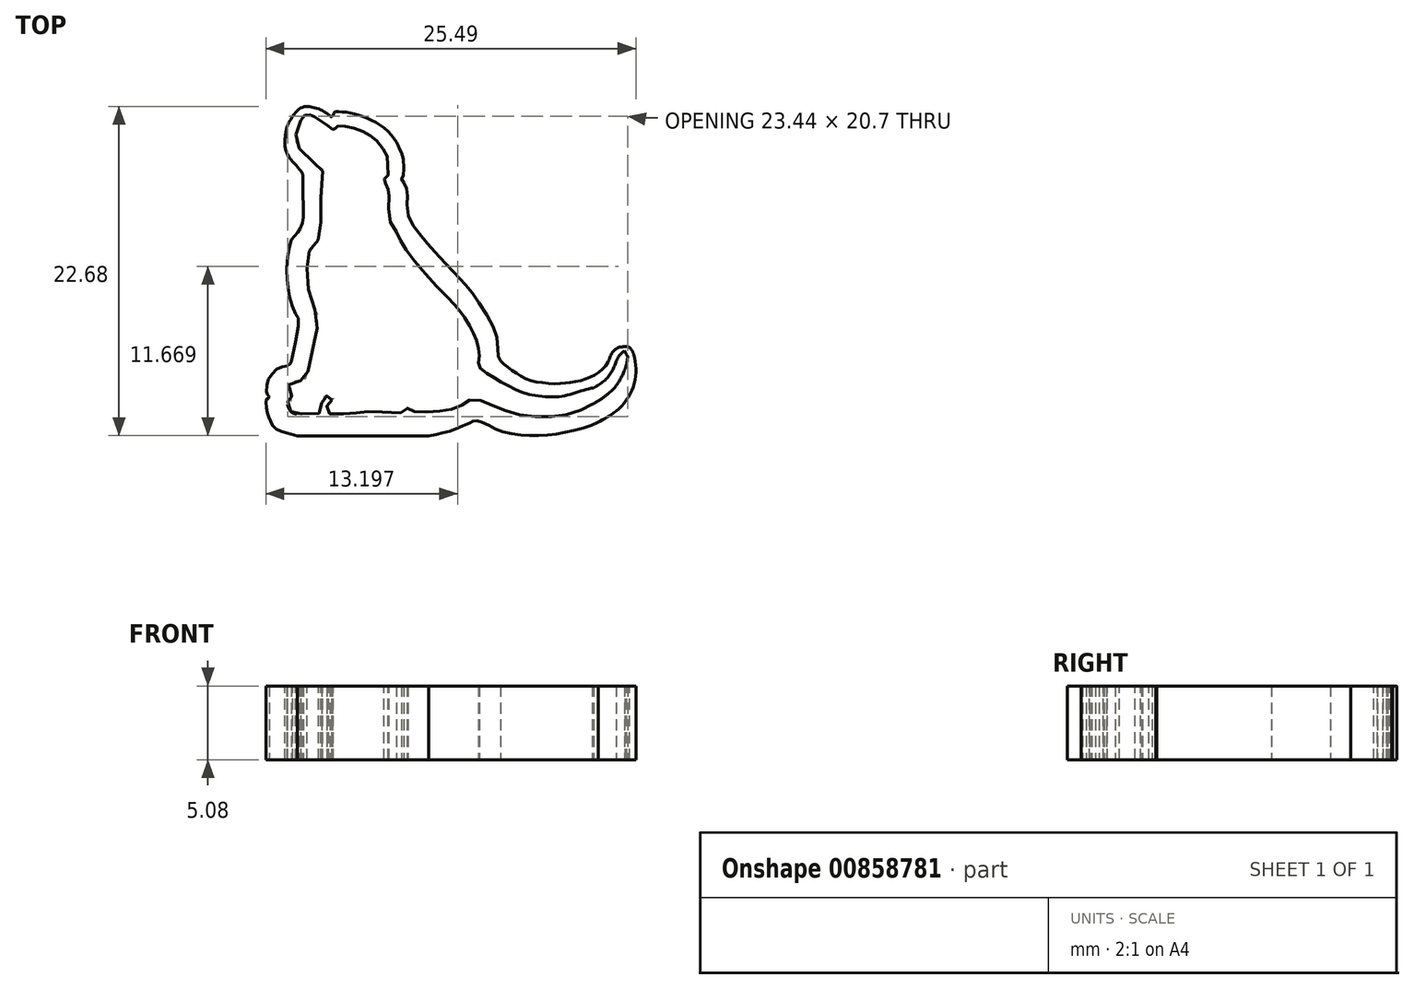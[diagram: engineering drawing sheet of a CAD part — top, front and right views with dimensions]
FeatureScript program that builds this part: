
annotation { "Feature Type Name" : "Feature", "Feature Type Description" : "" }
export const myFeature = defineFeature(function(context is Context, id is Id, definition is map)
    precondition{}
    {
        {
            var Q0;
            Q0=qCreatedBy(makeId("Top.planeOp"),FACE);
            var sketch = newSketch(context, id + "F0", { "sketchPlane" : qUnion([Q0])});
            skFitSpline(sketch, "E0", {"points": [v(-18.64, 26.8) * mm, v(-17.67, 25.17) * mm, v(-15, 22.17) * mm, v(-14.18, 21.25) * mm, v(-13.45, 20.1) * mm, v(-13.07, 19.16) * mm, v(-12.93, 18.19) * mm, v(-12.96, 17.55) * mm, v(-12.13, 16.92) * mm, v(-11.21, 16.35) * mm, v(-10.31, 15.9) * mm, v(-9.5, 15.6) * mm, v(-8.22, 15.45) * mm, v(-7.3, 15.48) * mm, v(-6.28, 15.74) * mm, v(-5.41, 16) * mm, v(-4.68, 16.04) * mm, v(-4.2, 15.74) * mm, v(-4.11, 15.31) * mm, v(-4.47, 14.84) * mm], "startDerivative": vector(10.05, -20.8) * mm, "endDerivative": vector(-11.78, -11.66) * mm});
            skFitSpline(sketch, "E1", {"points": [v(-9.5, 15.6) * mm, v(-8.72, 15.47) * mm, v(-7.72, 15.38) * mm, v(-6.88, 15.45) * mm, v(-6.21, 15.6) * mm, v(-5.62, 15.8) * mm, v(-5.06, 15.91) * mm, v(-4.74, 15.84) * mm, v(-4.58, 15.6) * mm, v(-4.64, 15.45) * mm, v(-4.81, 15.22) * mm, v(-5.13, 14.94) * mm, v(-5.65, 14.65) * mm, v(-6.3, 14.4) * mm, v(-7.1, 14.19) * mm, v(-7.82, 14.1) * mm, v(-8.74, 14.07) * mm, v(-9.5, 14.11) * mm, v(-10.51, 14.3) * mm, v(-11.1, 14.5) * mm, v(-11.64, 14.71) * mm, v(-12.33, 15) * mm, v(-12.8, 15.2) * mm, v(-13.18, 15.28) * mm, v(-13.65, 15.21) * mm, v(-13.89, 15.06) * mm, v(-14.13, 14.88) * mm, v(-14.44, 14.71) * mm, v(-14.94, 14.56) * mm, v(-15.47, 14.48) * mm, v(-16.02, 14.43) * mm, v(-16.6, 14.4) * mm, v(-17.18, 14.43) * mm, v(-17.55, 14.5) * mm, v(-17.68, 14.65) * mm, v(-17.88, 14.66) * mm, v(-17.96, 14.47) * mm, v(-18.17, 14.36) * mm, v(-19.22, 14.37) * mm, v(-20.18, 14.41) * mm, v(-20.7, 14.43) * mm, v(-21.2, 14.36) * mm, v(-21.69, 14.3) * mm, v(-22.28, 14.26) * mm, v(-23, 14.28) * mm, v(-23.35, 14.32) * mm, v(-23.43, 14.63) * mm, v(-23.4, 14.91) * mm, v(-23.24, 15.12) * mm, v(-23.07, 15.23) * mm], "startDerivative": vector(23.7, -7.27) * mm, "endDerivative": vector(13.55, 6.78) * mm});
            skFitSpline(sketch, "E2", {"points": [v(-18.64, 26.8) * mm, v(-19.13, 27.71) * mm, v(-19.15, 29.17) * mm, v(-19.16, 29.6) * mm, v(-19.26, 29.95) * mm, v(-19.43, 30.25) * mm, v(-19.49, 30.38) * mm, v(-19.43, 30.5) * mm, v(-19.26, 30.6) * mm, v(-19.2, 31.05) * mm, v(-19.26, 31.93) * mm, v(-19.33, 32.16) * mm, v(-19.82, 32.9) * mm, v(-20.2, 33.28) * mm, v(-20.67, 33.61) * mm, v(-21.2, 33.84) * mm, v(-21.83, 34.02) * mm, v(-22.38, 34.1) * mm, v(-22.69, 34.1) * mm, v(-22.78, 34.08) * mm, v(-22.83, 34) * mm, v(-22.85, 33.9) * mm, v(-22.92, 33.87) * mm, v(-23.02, 33.88) * mm, v(-23.16, 33.98) * mm, v(-24.31, 34.78) * mm, v(-24.49, 34.85) * mm, v(-24.67, 34.9) * mm, v(-24.86, 34.88) * mm, v(-25.01, 34.78) * mm, v(-25.2, 34.53) * mm, v(-25.25, 34.43) * mm, v(-25.24, 34.3) * mm, v(-25.23, 34.18) * mm], "startDerivative": vector(-11.38, 14.65) * mm, "endDerivative": vector(0.42, -6.75) * mm});
            skFitSpline(sketch, "E3", {"points": [v(-25.2, 34.53) * mm, v(-25.43, 34.12) * mm, v(-25.55, 33.7) * mm, v(-25.57, 33.14) * mm, v(-25.47, 32.8) * mm, v(-25.05, 32.28) * mm, v(-24.37, 31.64) * mm, v(-23.88, 31.24) * mm, v(-23.75, 31.13) * mm, v(-23.71, 30.96) * mm, v(-23.81, 29.43) * mm, v(-23.83, 27.82) * mm, v(-23.86, 27.12) * mm, v(-23.99, 26.36) * mm, v(-24.2, 26) * mm, v(-24.5, 25.67) * mm, v(-24.72, 25.34) * mm, v(-24.79, 24.67) * mm, v(-24.75, 23.66) * mm, v(-24.68, 22.74) * mm, v(-24.45, 21.84) * mm, v(-24.06, 21.1) * mm, v(-24.02, 20.72) * mm, v(-24.75, 17.1) * mm, v(-24.88, 16.75) * mm, v(-25.02, 16.6) * mm, v(-25.46, 16.55) * mm, v(-25.84, 16.43) * mm, v(-26.05, 16.28) * mm, v(-26.1, 15.69) * mm, v(-25.95, 15.55) * mm, v(-25.8, 15.44) * mm, v(-25.8, 15.29) * mm, v(-25.91, 15.22) * mm, v(-26.08, 15.2) * mm, v(-26.14, 14.98) * mm, v(-26.1, 14.74) * mm, v(-25.97, 14.52) * mm, v(-25.8, 14.35) * mm, v(-25.63, 14.29) * mm, v(-25.36, 14.27) * mm, v(-24.45, 14.27) * mm, v(-24.02, 14.29) * mm, v(-23.87, 14.38) * mm, v(-23.84, 14.72) * mm, v(-23.78, 15.01) * mm, v(-23.63, 15.25) * mm, v(-23.6, 15.46) * mm, v(-23.52, 15.52) * mm, v(-23.34, 15.52) * mm, v(-23.16, 15.45) * mm, v(-22.98, 15.35) * mm, v(-23.07, 15.23) * mm], "startDerivative": vector(-12.69, -20.47) * mm, "endDerivative": vector(-12.96, -11.1) * mm});
            skFitSpline(sketch, "E4", {"points": [v(-23.08, 16.7) * mm, v(-21.94, 19.17) * mm, v(-21.85, 19.47) * mm, v(-21.79, 19.58) * mm, v(-21.64, 19.6) * mm, v(-21.56, 19.53) * mm, v(-21.54, 19.42) * mm, v(-21.46, 19.35) * mm, v(-21.26, 19.2) * mm, v(-21.06, 19.1) * mm, v(-20.96, 19.02) * mm, v(-20.97, 18.84) * mm, v(-21.11, 18.68) * mm, v(-21.16, 18.5) * mm, v(-21.17, 18.18) * mm, v(-21.1, 17.9) * mm, v(-20.94, 17.57) * mm, v(-20.66, 17.12) * mm, v(-20.63, 16.86) * mm, v(-20.8, 16.71) * mm, v(-21.1, 16.62) * mm, v(-21.6, 16.57) * mm, v(-22.32, 16.56) * mm, v(-22.93, 16.5) * mm, v(-23.08, 16.53) * mm, v(-23.13, 16.58) * mm, v(-23.08, 16.7) * mm]});
            skFitSpline(sketch, "E5", {"points": [v(-21.86, 15.57) * mm, v(-19.82, 15.8) * mm, v(-19.69, 15.8) * mm, v(-19.62, 15.6) * mm, v(-19.68, 15.5) * mm, v(-20.03, 15.34) * mm, v(-20.57, 15.23) * mm, v(-21.23, 15.2) * mm, v(-21.7, 15.28) * mm, v(-21.84, 15.34) * mm], "startDerivative": vector(10.76, 1.04) * mm, "endDerivative": vector(-1.73, 0.9) * mm});
            skFitSpline(sketch, "E6", {"points": [v(-21.84, 15.34) * mm, v(-21.88, 15.44) * mm, v(-21.86, 15.57) * mm], "startDerivative": vector(-0.1, 0.21) * mm, "endDerivative": vector(0.07, 0.25) * mm});
            skPoint(sketch, "E7.1.internal.orphan", {"position": v(-24.41, 31.05) * mm});
            skPoint(sketch, "E8.7.internal.snap0", {"position": v(-11.42, 13.4) * mm});
            skPoint(sketch, "E8.8.internal.snap0", {"position": v(-11.42, 13.45) * mm});
            skFitSpline(sketch, "E9.trimOffspring", {"points": [v(-11.33, 13.53) * mm, v(-12.83, 14.23) * mm, v(-13.03, 14.3) * mm, v(-13.4, 14.32) * mm, v(-13.63, 14.24) * mm, v(-14.53, 13.84) * mm, v(-15.5, 13.53) * mm, v(-18.01, 13.4) * mm, v(-24.51, 13.45) * mm, v(-26.14, 14.16) * mm], "startDerivative": vector(-14.88, 6.54) * mm, "endDerivative": vector(-9.16, 7.25) * mm});
            skFitSpline(sketch, "E10.trimOffspring", {"points": [v(-25.27, 17.31) * mm, v(-25.4, 17.12) * mm, v(-25.87, 17.05) * mm, v(-26.28, 16.9) * mm, v(-26.59, 16.65) * mm, v(-26.82, 16.2) * mm, v(-26.85, 15.72) * mm, v(-26.81, 15.56) * mm, v(-26.7, 15.48) * mm, v(-26.7, 15.43) * mm, v(-26.72, 15.35) * mm, v(-26.78, 15.29) * mm, v(-26.81, 15.27) * mm, v(-26.83, 15.23) * mm, v(-26.84, 15.17) * mm, v(-26.79, 14.82) * mm, v(-26.75, 14.37) * mm, v(-26.31, 13.9) * mm, v(-24.51, 13.45) * mm], "startDerivative": vector(-1.67, -4.49) * mm, "endDerivative": vector(14.6, -2.5) * mm});
            skFitSpline(sketch, "E11", {"points": [v(-6.48, 17.1) * mm, v(-7.36, 16.99) * mm, v(-8.18, 16.99) * mm, v(-9.04, 17.07) * mm, v(-9.92, 17.26) * mm, v(-10.74, 17.6) * mm, v(-11.45, 17.93) * mm, v(-11.59, 18.15) * mm, v(-11.63, 18.41) * mm, v(-11.7, 19.47) * mm, v(-12.19, 20.74) * mm, v(-13.2, 22.3) * mm, v(-13.91, 23.21) * mm, v(-16.3, 25.78) * mm, v(-17.26, 26.98) * mm, v(-17.78, 27.85) * mm, v(-17.88, 29.02) * mm, v(-17.86, 29.53) * mm, v(-18.02, 30.04) * mm, v(-18.2, 30.28) * mm, v(-18.27, 30.42) * mm, v(-18.25, 30.57) * mm, v(-18.17, 30.66) * mm, v(-18.13, 31.07) * mm, v(-18.18, 31.92) * mm, v(-18.28, 32.28) * mm, v(-18.85, 33.1) * mm, v(-19.38, 33.72) * mm, v(-20.14, 34.24) * mm, v(-20.86, 34.57) * mm, v(-21.64, 34.79) * mm, v(-22.34, 34.89) * mm, v(-22.74, 34.9) * mm, v(-22.87, 34.85) * mm, v(-22.9, 34.77) * mm, v(-22.92, 34.69) * mm, v(-22.94, 34.61) * mm, v(-23.03, 34.57) * mm, v(-23.1, 34.57) * mm, v(-23.2, 34.63) * mm, v(-23.38, 34.79) * mm], "startDerivative": vector(-28.78, -4.16) * mm, "endDerivative": vector(-12.37, 11.09) * mm});
            skFitSpline(sketch, "E12", {"points": [v(-18.28, 32.28) * mm, v(-18.57, 32.86) * mm, v(-19, 33.53) * mm, v(-19.88, 34.26) * mm, v(-20.7, 34.66) * mm, v(-21.58, 34.97) * mm, v(-22.33, 35.08) * mm, v(-22.76, 35.1) * mm, v(-22.88, 35.07) * mm, v(-22.95, 34.96) * mm, v(-23, 34.85) * mm, v(-23.04, 34.78) * mm, v(-23.12, 34.77) * mm, v(-23.16, 34.77) * mm, v(-23.22, 34.84) * mm, v(-23.3, 34.9) * mm, v(-23.53, 35.07) * mm], "startDerivative": vector(-3.23, 6.6) * mm, "endDerivative": vector(-4.35, 3.68) * mm});
            skFitSpline(sketch, "E13", {"points": [v(-23.04, 34.78) * mm, v(-23.06, 34.77) * mm, v(-23.1, 34.77) * mm, v(-23.14, 34.79) * mm, v(-23.4, 34.97) * mm, v(-23.76, 35.18) * mm, v(-24.11, 35.43) * mm, v(-24.54, 35.57) * mm, v(-24.95, 35.59) * mm, v(-25.4, 35.53) * mm, v(-25.8, 35.28) * mm, v(-26.19, 34.91) * mm, v(-26.45, 34.47) * mm, v(-26.72, 33.71) * mm, v(-26.75, 32.98) * mm, v(-26.57, 32.2) * mm, v(-26.07, 31.53) * mm, v(-25.4, 31) * mm, v(-25.12, 30.88) * mm, v(-25.08, 30.74) * mm, v(-25.07, 30.57) * mm, v(-25.07, 29.48) * mm, v(-25.05, 27.86) * mm, v(-25.12, 27.36) * mm, v(-25.28, 27.01) * mm, v(-25.4, 26.8) * mm, v(-25.6, 26.59) * mm, v(-25.8, 26.4) * mm, v(-25.95, 25.99) * mm, v(-26.1, 25.28) * mm, v(-26.17, 24.68) * mm, v(-26.15, 23.63) * mm, v(-26.07, 22.7) * mm, v(-25.8, 21.62) * mm, v(-25.47, 21.02) * mm, v(-25.37, 20.78) * mm, v(-25.88, 17.9) * mm], "startDerivative": vector(-3.52, -1.33) * mm, "endDerivative": vector(-12.4, -56.43) * mm});
            skFitSpline(sketch, "E14", {"points": [v(-25.88, 17.9) * mm, v(-25.93, 17.73) * mm, v(-26.03, 17.63) * mm, v(-26.34, 17.56) * mm, v(-26.8, 17.41) * mm, v(-27.3, 16.88) * mm, v(-27.55, 16.35) * mm, v(-27.58, 15.74) * mm, v(-27.54, 15.61) * mm, v(-27.45, 15.55) * mm, v(-27.42, 15.51) * mm, v(-27.42, 15.42) * mm, v(-27.48, 15.34) * mm, v(-27.53, 15.31) * mm, v(-27.6, 15.28) * mm, v(-27.62, 15.2) * mm, v(-27.6, 14.84) * mm, v(-27.54, 14.37) * mm, v(-27.46, 14.1) * mm, v(-27.33, 13.82) * mm, v(-27.18, 13.48) * mm, v(-26.9, 13.22) * mm, v(-26.42, 13.01) * mm, v(-26.1, 12.92) * mm, v(-25.44, 12.77) * mm], "startDerivative": vector(-1.3, -5.64) * mm, "endDerivative": vector(11.14, -2.6) * mm});
            skLineSegment(sketch, "E15", {"start": v(-25.44, 12.77) * mm, "end": v(-16.4, 12.77) * mm});
            skFitSpline(sketch, "E16", {"points": [v(-16.4, 12.77) * mm, v(-15.63, 12.92) * mm, v(-15, 13.08) * mm, v(-14.33, 13.31) * mm, v(-13.57, 13.67) * mm, v(-13.43, 13.74) * mm, v(-13.13, 13.8) * mm, v(-12.95, 13.77) * mm, v(-12.2, 13.45) * mm, v(-11.48, 13.1) * mm, v(-10.27, 12.85) * mm, v(-9.14, 12.77) * mm, v(-7.98, 12.84) * mm, v(-6.82, 13.04) * mm, v(-5.6, 13.35) * mm, v(-4.74, 13.7) * mm, v(-4.16, 13.95) * mm, v(-3.3, 14.47) * mm, v(-2.28, 15.31) * mm], "startDerivative": vector(14.64, 2.55) * mm, "endDerivative": vector(13.76, 11.69) * mm});
            skFitSpline(sketch, "E17.trimOffspring", {"points": [v(-23.04, 34.78) * mm, v(-23.06, 34.77) * mm, v(-23.1, 34.77) * mm, v(-23.14, 34.79) * mm, v(-23.4, 34.97) * mm, v(-23.76, 35.18) * mm, v(-24.11, 35.43) * mm, v(-24.54, 35.57) * mm, v(-24.95, 35.59) * mm, v(-25.4, 35.53) * mm, v(-25.8, 35.28) * mm, v(-26.19, 34.91) * mm, v(-26.45, 34.47) * mm, v(-26.72, 33.71) * mm, v(-26.75, 32.98) * mm, v(-26.57, 32.2) * mm, v(-26.07, 31.53) * mm, v(-25.4, 31) * mm, v(-25.12, 30.88) * mm, v(-25.08, 30.74) * mm, v(-25.07, 30.57) * mm, v(-25.07, 29.48) * mm, v(-25.05, 27.86) * mm, v(-25.12, 27.36) * mm, v(-25.28, 27.01) * mm, v(-25.4, 26.8) * mm, v(-25.6, 26.59) * mm, v(-25.8, 26.4) * mm, v(-25.95, 25.99) * mm, v(-26.1, 25.28) * mm, v(-26.17, 24.68) * mm, v(-26.15, 23.63) * mm, v(-26.07, 22.7) * mm, v(-25.8, 21.62) * mm, v(-25.47, 21.02) * mm, v(-25.37, 20.78) * mm, v(-25.88, 17.9) * mm], "startDerivative": vector(-3.52, -1.33) * mm, "endDerivative": vector(-12.4, -56.43) * mm});
            skFitSpline(sketch, "E18", {"points": [v(-26.15, 34.12) * mm, v(-26.08, 34.28) * mm, v(-25.97, 34.48) * mm, v(-25.83, 34.71) * mm, v(-25.67, 34.93) * mm, v(-25.43, 35.2) * mm, v(-25.21, 35.36) * mm, v(-24.98, 35.44) * mm, v(-24.8, 35.45) * mm, v(-24.63, 35.44) * mm, v(-24.43, 35.41) * mm, v(-24.2, 35.35) * mm, v(-23.93, 35.27) * mm, v(-23.76, 35.18) * mm], "startDerivative": vector(1.03, 2.42) * mm, "endDerivative": vector(3.44, -1.92) * mm});
            skFitSpline(sketch, "E19", {"points": [v(-25.12, 30.88) * mm, v(-25.24, 31.05) * mm, v(-25.58, 31.42) * mm, v(-26.06, 32.01) * mm, v(-26.3, 32.58) * mm, v(-26.32, 33.06) * mm, v(-26.25, 33.67) * mm, v(-26.15, 34.12) * mm], "startDerivative": vector(-1.17, 1.7) * mm, "endDerivative": vector(0.8, 3.11) * mm});
            skLineSegment(sketch, "E20", {"start": v(-5.13, 14.94) * mm, "end": v(-4.98, 14.75) * mm});
            skLineSegment(sketch, "E21", {"start": v(-5.13, 14.94) * mm, "end": v(-5.25, 15.08) * mm});
            skLineSegment(sketch, "E22", {"start": v(-11.45, 17.93) * mm, "end": v(-11.27, 18.13) * mm});
            skLineSegment(sketch, "E23", {"start": v(-11.45, 17.93) * mm, "end": v(-11.67, 17.7) * mm});
            skFitSpline(sketch, "E24", {"points": [v(-11.45, 17.93) * mm, v(-11.1, 17.6) * mm, v(-10.53, 17.18) * mm, v(-9.97, 16.83) * mm, v(-9.33, 16.55) * mm, v(-8.54, 16.42) * mm, v(-7.67, 16.35) * mm, v(-6.99, 16.4) * mm, v(-6.4, 16.48) * mm, v(-5.7, 16.64) * mm, v(-5.21, 16.84) * mm, v(-4.75, 17.1) * mm, v(-4.32, 17.46) * mm, v(-4.06, 17.83) * mm, v(-3.85, 18.33) * mm, v(-3.62, 18.66) * mm, v(-3.34, 18.84) * mm, v(-3.05, 18.9) * mm, v(-2.79, 18.9) * mm, v(-2.57, 18.85) * mm, v(-2.45, 18.6) * mm, v(-2.42, 18.16) * mm, v(-2.45, 17.6) * mm, v(-2.53, 17.03) * mm], "startDerivative": vector(7.84, -7.71) * mm, "endDerivative": vector(-1.96, -12.26) * mm});
            skFitSpline(sketch, "E25", {"points": [v(-5.62, 15.8) * mm, v(-5.17, 16) * mm, v(-4.74, 16.25) * mm, v(-4.32, 16.56) * mm, v(-3.94, 16.96) * mm, v(-3.65, 17.49) * mm, v(-3.49, 17.88) * mm, v(-3.31, 18.22) * mm, v(-3.18, 18.36) * mm, v(-3.03, 18.4) * mm, v(-2.85, 18.4) * mm, v(-2.76, 18.33) * mm, v(-2.71, 18.24) * mm, v(-2.71, 18.09) * mm, v(-2.73, 17.96) * mm, v(-2.8, 17.76) * mm], "startDerivative": vector(5.23, 2.04) * mm, "endDerivative": vector(-1.4, -3.71) * mm});
            skFitSpline(sketch, "E26", {"points": [v(-5.13, 14.94) * mm, v(-4.9, 15.07) * mm, v(-4.56, 15.28) * mm, v(-4.24, 15.52) * mm, v(-3.83, 15.85) * mm, v(-3.45, 16.28) * mm, v(-3.16, 16.75) * mm, v(-2.9, 17.3) * mm, v(-2.73, 17.96) * mm], "startDerivative": vector(2.45, 1.27) * mm, "endDerivative": vector(0.98, 4.52) * mm});
            skLineSegment(sketch, "E27", {"start": v(-3.49, 17.88) * mm, "end": v(-3.62, 17.94) * mm});
            skLineSegment(sketch, "E28", {"start": v(-3.49, 17.88) * mm, "end": v(-3.35, 17.82) * mm});
            skLineSegment(sketch, "E29", {"start": v(-2.9, 17.3) * mm, "end": v(-2.82, 17.28) * mm});
            skLineSegment(sketch, "E30", {"start": v(-2.9, 17.3) * mm, "end": v(-3, 17.34) * mm});
            skFitSpline(sketch, "E31", {"points": [v(-3.49, 17.88) * mm, v(-3.42, 18.05) * mm, v(-3.36, 18.18) * mm, v(-3.22, 18.37) * mm, v(-3.07, 18.51) * mm, v(-2.9, 18.61) * mm], "startDerivative": vector(0.32, 0.9) * mm, "endDerivative": vector(0.83, 0.47) * mm});
            skFitSpline(sketch, "E32", {"points": [v(-2.9, 17.3) * mm, v(-2.84, 17.49) * mm, v(-2.78, 17.69) * mm, v(-2.75, 17.92) * mm, v(-2.74, 18.1) * mm, v(-2.75, 18.2) * mm, v(-2.8, 18.39) * mm, v(-2.86, 18.54) * mm, v(-2.9, 18.61) * mm], "startDerivative": vector(0.45, 1.34) * mm, "endDerivative": vector(-0.44, 0.75) * mm});
            skFitSpline(sketch, "E33", {"points": [v(-4.74, 13.7) * mm, v(-4.41, 13.87) * mm, v(-3.93, 14.16) * mm, v(-3.35, 14.58) * mm, v(-2.86, 15.13) * mm, v(-2.43, 15.85) * mm, v(-2.2, 16.6) * mm, v(-2.13, 17.4) * mm, v(-2.22, 18.12) * mm, v(-2.34, 18.51) * mm, v(-2.45, 18.71) * mm, v(-2.57, 18.85) * mm], "startDerivative": vector(4.17, 2.2) * mm, "endDerivative": vector(-2.37, 2.44) * mm});
            skLineSegment(sketch, "E34", {"start": v(-4.06, 17.83) * mm, "end": v(-4.26, 17.92) * mm});
            skLineSegment(sketch, "E35", {"start": v(-4.06, 17.83) * mm, "end": v(-3.86, 17.74) * mm});
            skLineSegment(sketch, "E36", {"start": v(-2.22, 18.12) * mm, "end": v(-2, 18.12) * mm});
            skLineSegment(sketch, "E37", {"start": v(-2.22, 18.12) * mm, "end": v(-2.33, 18.12) * mm});
            skPoint(sketch, "E38.1.internal.snap0", {"position": v(-3.96, 17.78) * mm});
            skFitSpline(sketch, "E38", {"points": [v(-4.06, 17.83) * mm, v(-3.96, 18.14) * mm, v(-3.79, 18.6) * mm, v(-3.53, 19.01) * mm, v(-3.18, 19.32) * mm, v(-2.85, 19.54) * mm], "startDerivative": vector(0.54, 1.72) * mm, "endDerivative": vector(1.7, 1.08) * mm});
            skFitSpline(sketch, "E39", {"points": [v(-2.22, 18.12) * mm, v(-2.26, 18.35) * mm, v(-2.33, 18.66) * mm, v(-2.41, 18.99) * mm, v(-2.53, 19.3) * mm, v(-2.66, 19.48) * mm, v(-2.7, 19.53) * mm, v(-2.79, 19.56) * mm, v(-2.85, 19.54) * mm], "startDerivative": vector(-0.23, 1.58) * mm, "endDerivative": vector(-0.75, -0.43) * mm});
            skSolve(sketch);
        }
        {
            var Q0;
            Q0=makeQuery(id+"F0.imprint","IMPRINT",FACE,{"disambiguationData":[TD([[makeQuery(id+"F0.imprint","IMPRINT",EDGE,{"derivedFrom":sQuery(id+"F0.wireOp",EDGE,"E0")}),1.0]])]});
            extrude(context, id + "F1", {"entities" : qUnion([Q0]), "offsetDistance" : 25 * mm, "depth" : 5.08 * mm});
        }
    });
